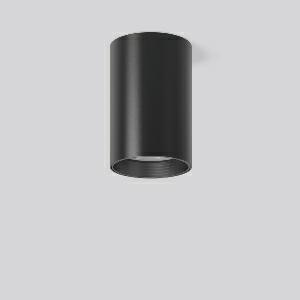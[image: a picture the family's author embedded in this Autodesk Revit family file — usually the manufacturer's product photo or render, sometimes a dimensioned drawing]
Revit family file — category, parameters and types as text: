
# Revit family: heledon_maxi_a_931229_003_6a87
name_source: partatom
category: Lighting Fixtures
units: mm (PartAtom-declared; Revit-internal decimal feet)

## family parameters
Cut with Voids When Loaded = No
Host = Face
Light Source = No
Part Type = Normal
Room Calculation Point = No
Round Connector Dimension = Use Diameter
Shared = No

## types (1)
- HELEDON maxi A (1 x LED Modul 930, 3600 lm, 3000)
    Apparent Load = 35 VA
    Approval mark = CE
    CIE Flux Codes = 96 100 100 100 100
    Color Rendering = 90
    Color Temperature = 3000
    Default Elevation = 1800 mm
    Description = Series: HELEDON maxi
Cylindrical surface-mounted downlight. Housing: die-cast aluminium, powder-coated. Internal ceiling frame polycarbonate with bayonet mounting. Black plastic ring and recessed LED to prevent glare from the side. Optical assembly with lens made of plastic (polycarbonate) for the best homogeneous light distribution - can be changed without tools. Best colour rendering index Ra>90. Suitable for Ceiling mounting. Easy installation with a separate ceiling frame with bayonet mounting and plug connection. Driver integrated. Connected via plug-in connector. High quality converter without flickering and stroboscopic effect. The following accessories can be mounted without use of tools: interchangeable lenses, decorative glasses, honeycomb louvre, clear and frosted diffusers, white interchangeable plastic ring. 
Colour: deep black, matt (RAL 9005)
Diameter: 123 mm
Height: 183 mm
Lamp: LED
Socket: without socket
Colour temperature: 3000K
Colour rendering index (CRI): 92
System power: 35 W
Rated luminous flux: 3600 lm
Luminous efficiency: 103 lm/W
Control gear: Regulated power supply
Protection class: I
Type of protection: IP 20
    Height = 183 mm
    Lamp = 1 x LED Modul 930
    Lamp Light Flux = 3600 lm
    Lamp count = 1
    Length = 123 mm
    Lifetime = 50000 h
    Luminous efficacy = 103 lm/W
    Manufacturer = RZB
    ModVariant = No
    Model = 931229.003
    Mounting Place = Ceiling
    Mounting Type = Surface mounted
    Number of Poles = 1
    OnlyDefault = Yes
    Power Factor = 1
    Product Name = HELEDON maxi A
    Product group = Surface mounted downlights
    ProductGroupID = 302
    Protection Class = Protection class I
    Protection Degree = IP 20
    RLX_Detail_Level = 1
    RLX_Emergency_Light_Flux = 0 lm
    RLX_Emergency_Type = 0
    RLX_Emergency_Type_DB = No
    RlxData = <blob elided: 96129 chars, md5=d1dd6ac5>
    Socket = socket
    Standby Power = 0 W
    System Light Flux = 3600 lm
    System Power = 35 W
    Type Comments = Product without accessories
    Type Image = 931193.003.jpg
    URL = http://relux.com
    VarID = ---
    Voltage = 230 V
    Voltage Range = 220-240 V
    Weight = 0.00 kg
    Width = 0 mm  [stored 0 ft]

note: [stored X ft] marks values corroborated as IEEE doubles in the binary element streams (Revit-internal decimal feet)

## geometry (parser evidence)
native form markers: Blend x4, Sweep x10
no freeform markers — native parametric forms only
